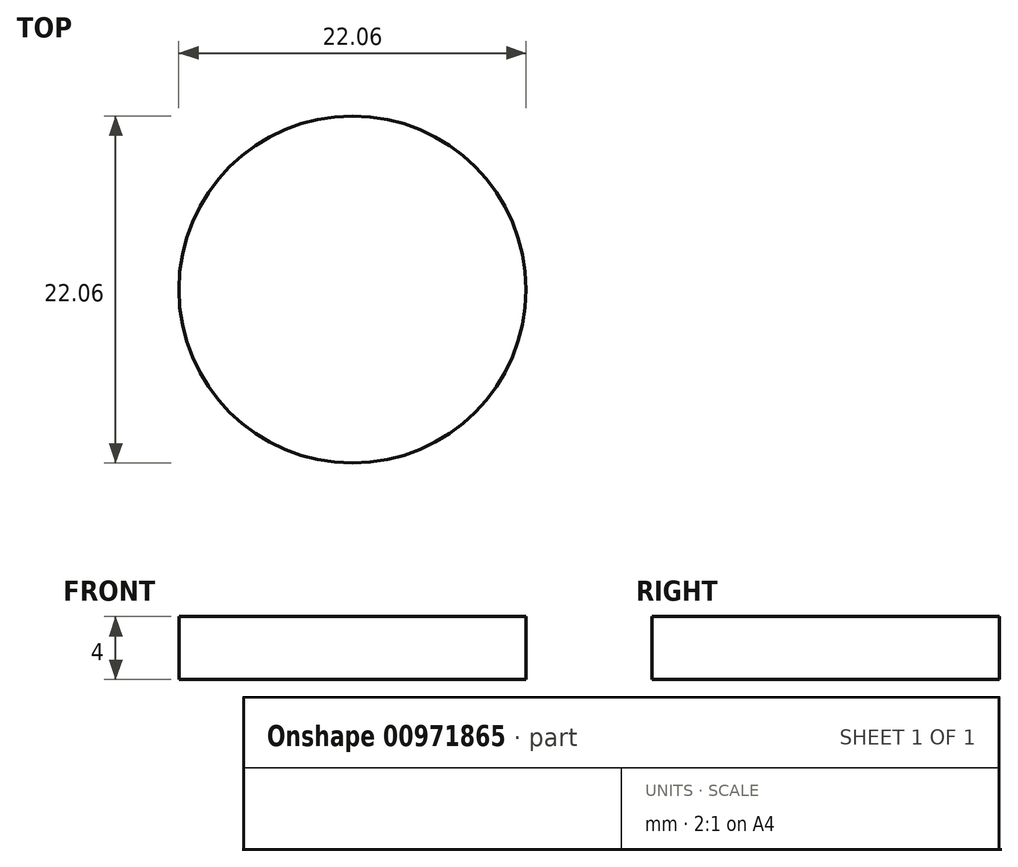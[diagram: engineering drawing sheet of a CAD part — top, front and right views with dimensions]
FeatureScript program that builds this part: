
annotation { "Feature Type Name" : "Feature", "Feature Type Description" : "" }
export const myFeature = defineFeature(function(context is Context, id is Id, definition is map)
    precondition{}
    {
        {
            var Q0;
            Q0=qCreatedBy(makeId("Top.planeOp"),FACE);
            var sketch = newSketch(context, id + "F0", { "sketchPlane" : qUnion([Q0])});
            skCircle(sketch, "E0", {"center": v(0, 0) * mm, "radius": 279.4 * mm});
            skCircle(sketch, "E1", {"center": v(0, 0) * mm, "radius": 11.03 * mm});
            skCircle(sketch, "E2", {"center": v(0, 0) * mm, "radius": 3 * mm});
            skSolve(sketch);
        }
        {
            var Q0;
            Q0=makeQuery(id+"F0.imprint","IMPRINT",FACE,{"disambiguationData":[TD([[makeQuery(id+"F0.imprint","IMPRINT",EDGE,{"derivedFrom":sQuery(id+"F0.wireOp",EDGE,"E1")}),1.0]])]});
            var Q1;
            Q1=makeQuery(id+"F0.imprint","IMPRINT",FACE,{"disambiguationData":[TD([[makeQuery(id+"F0.imprint","IMPRINT",EDGE,{"derivedFrom":sQuery(id+"F0.wireOp",EDGE,"E2")}),1.0]])]});
            extrude(context, id + "F1", {"entities" : qUnion([Q0, Q1]), "depth" : 4 * mm, "offsetDistance" : 25 * mm});
        }
    });
